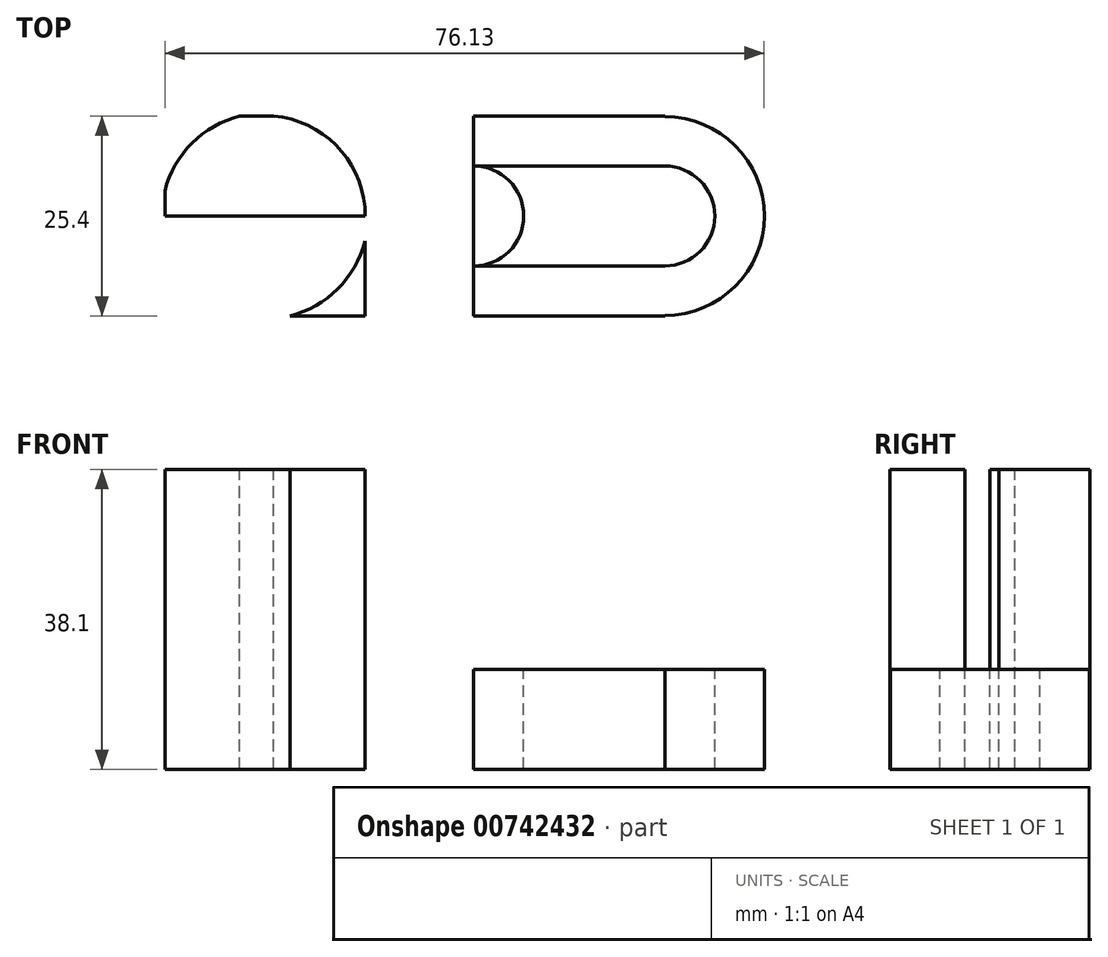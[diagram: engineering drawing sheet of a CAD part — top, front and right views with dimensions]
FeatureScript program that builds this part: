
annotation { "Feature Type Name" : "Feature", "Feature Type Description" : "" }
export const myFeature = defineFeature(function(context is Context, id is Id, definition is map)
    precondition{}
    {
        {
            var Q0;
            Q0=qCreatedBy(makeId("Front.planeOp"),FACE);
            var sketch = newSketch(context, id + "F0", { "sketchPlane" : qUnion([Q0])});
            skLineSegment(sketch, "E0", {"start": v(0, 38.1) * mm, "end": v(0, 0) * mm});
            skLineSegment(sketch, "E1", {"start": v(0, 0) * mm, "end": v(76.2, 0) * mm});
            skLineSegment(sketch, "E2", {"start": v(76.2, 0) * mm, "end": v(76.2, 12.7) * mm});
            skLineSegment(sketch, "E3", {"start": v(76.2, 12.7) * mm, "end": v(25.4, 12.7) * mm});
            skLineSegment(sketch, "E4", {"start": v(25.4, 12.7) * mm, "end": v(25.4, 38.1) * mm});
            skLineSegment(sketch, "E5", {"start": v(25.4, 38.1) * mm, "end": v(0, 38.1) * mm});
            skSolve(sketch);
        }
        {
            var Q0;
            Q0 = qSketchRegion(id + "F0", true);
            extrude(context, id + "F1", {"entities" : qUnion([Q0]), "depth" : 25.4 * mm, "offsetDistance" : 25.4 * mm});
        }
        {
            var Q0;
            Q0=makeQuery(id+"F1.opExtrude","SWEPT_FACE",FACE,{"disambiguationData":[OSD([sQuery(id+"F0.wireOp",EDGE,"E5")])]});
            var sketch = newSketch(context, id + "F2", { "sketchPlane" : qUnion([Q0])});
            skLineSegment(sketch, "E6", {"start": v(12.7, 0) * mm, "end": v(12.7, -25.4) * mm});
            skLineSegment(sketch, "E7", {"start": v(0, -12.7) * mm, "end": v(25.4, -12.7) * mm});
            skCircle(sketch, "E8", {"center": v(12.7, -12.7) * mm, "radius": 13.1 * mm});
            skCircle(sketch, "E9", {"center": v(12.7, -12.7) * mm, "radius": 6.35 * mm});
            skSolve(sketch);
        }
        {
            var Q0;
            {var subQ0=sQuery(id+"F2.wireOp",EDGE,"E9");var subQ1=sQuery(id+"F2.wireOp",EDGE,"E6");var subQ2=makeQuery(id+"F2.imprint","INTERSECT",VERTEX,{"disambiguationData":[OD(0.0)],"derivedFrom":[subQ1,subQ0]});Q0=makeQuery(id+"F2.imprint","IMPRINT",FACE,{"disambiguationData":[TD([[makeQuery(id+"F2.imprint","IMPRINT",EDGE,{"disambiguationData":[TD([[subQ2,-1.0]])],"derivedFrom":subQ1}),-1.0]])]});}
            var Q1;
            {var subQ0=sQuery(id+"F2.wireOp",EDGE,"E9");var subQ1=sQuery(id+"F2.wireOp",EDGE,"E6");var subQ2=makeQuery(id+"F2.imprint","INTERSECT",VERTEX,{"disambiguationData":[OD(0.0)],"derivedFrom":[subQ1,subQ0]});Q1=makeQuery(id+"F2.imprint","IMPRINT",FACE,{"disambiguationData":[TD([[makeQuery(id+"F2.imprint","IMPRINT",EDGE,{"disambiguationData":[TD([[subQ2,-1.0]])],"derivedFrom":subQ1}),1.0]])]});}
            var Q2;
            {var subQ0=sQuery(id+"F2.wireOp",EDGE,"E7");var subQ1=sQuery(id+"F2.wireOp",EDGE,"E6");var subQ2=makeQuery(id+"F2.imprint","INTERSECT",VERTEX,{"derivedFrom":[subQ1,subQ0]});Q2=makeQuery(id+"F2.imprint","IMPRINT",FACE,{"disambiguationData":[TD([[makeQuery(id+"F2.imprint","IMPRINT",EDGE,{"disambiguationData":[TD([[subQ2,-1.0]])],"derivedFrom":subQ1}),1.0]])]});}
            var Q3;
            {var subQ0=sQuery(id+"F2.wireOp",EDGE,"E7");var subQ1=sQuery(id+"F2.wireOp",EDGE,"E6");var subQ2=makeQuery(id+"F2.imprint","INTERSECT",VERTEX,{"derivedFrom":[subQ1,subQ0]});Q3=makeQuery(id+"F2.imprint","IMPRINT",FACE,{"disambiguationData":[TD([[makeQuery(id+"F2.imprint","IMPRINT",EDGE,{"disambiguationData":[TD([[subQ2,-1.0]])],"derivedFrom":subQ1}),-1.0]])]});}
            var Q4;
            {var subQ0=sQuery(id+"F2.wireOp",EDGE,"E8");var subQ1=sQuery(id+"F0.wireOp",EDGE,"E5");var subQ2=makeQuery(id+"F1.opExtrude","CAP_EDGE",EDGE,{"disambiguationData":[OSD([subQ1])],"isStart":true});var subQ3=makeQuery(id+"F2.imprint","INTERSECT",VERTEX,{"disambiguationData":[OD(1.0)],"derivedFrom":[subQ2,subQ0]});Q4=makeQuery(id+"F2.imprint","IMPRINT",FACE,{"disambiguationData":[TD([[makeQuery(id+"F2.imprint","IMPRINT",EDGE,{"disambiguationData":[TD([[subQ3,-1.0]])],"derivedFrom":subQ0}),-1.0]])]});}
            var Q5;
            {var subQ0=sQuery(id+"F2.wireOp",EDGE,"E8");var subQ1=sQuery(id+"F0.wireOp",EDGE,"E5");var subQ4=makeQuery(id+"F1.opExtrude","CAP_EDGE",EDGE,{"disambiguationData":[OSD([subQ1])],"isStart":false});var subQ5=makeQuery(id+"F2.imprint","INTERSECT",VERTEX,{"disambiguationData":[OD(0.0)],"derivedFrom":[subQ4,subQ0]});Q5=makeQuery(id+"F2.imprint","IMPRINT",FACE,{"disambiguationData":[TD([[makeQuery(id+"F2.imprint","IMPRINT",EDGE,{"disambiguationData":[TD([[subQ5,1.0]])],"derivedFrom":subQ0}),-1.0]])]});}
            extrude(context, id + "F3", {"entities" : qUnion([Q0, Q1, Q2, Q3, Q4, Q5]), "operationType" : NewBodyOperationType.REMOVE, "endBound" : BoundingType.THROUGH_ALL, "oppositeDirection" : true, "depth" : 25.4 * mm, "offsetDistance" : 25.4 * mm});
        }
        {
            var Q0;
            Q0=makeQuery(id+"F1.opExtrude","SWEPT_FACE",FACE,{"disambiguationData":[OSD([sQuery(id+"F0.wireOp",EDGE,"E5")])]});
            var sketch = newSketch(context, id + "F4", { "sketchPlane" : qUnion([Q0])});
            skLineSegment(sketch, "E10", {"start": v(0, 0) * mm, "end": v(12.7, 0) * mm});
            skLineSegment(sketch, "E11", {"start": v(12.7, 0) * mm, "end": v(12.7, -25.4) * mm});
            skLineSegment(sketch, "E12", {"start": v(0, -12.7) * mm, "end": v(25.4, -12.7) * mm});
            skCircle(sketch, "E13", {"center": v(12.7, -12.7) * mm, "radius": 12.75 * mm});
            skSolve(sketch);
        }
        {
            var Q0;
            {var subQ0=sQuery(id+"F4.wireOp",EDGE,"E13");var subQ1=sQuery(id+"F0.wireOp",EDGE,"E5");var subQ2=makeQuery(id+"F1.opExtrude","CAP_EDGE",EDGE,{"disambiguationData":[OSD([subQ1])],"isStart":false});var subQ3=makeQuery(id+"F4.imprint","INTERSECT",VERTEX,{"disambiguationData":[OD(1.0)],"derivedFrom":[subQ2,subQ0]});Q0=makeQuery(id+"F4.imprint","IMPRINT",FACE,{"disambiguationData":[TD([[makeQuery(id+"F4.imprint","IMPRINT",EDGE,{"disambiguationData":[TD([[subQ3,-1.0]])],"derivedFrom":subQ0}),-1.0]])]});}
            var Q1;
            {var subQ0=sQuery(id+"F4.wireOp",EDGE,"E13");var subQ1=sQuery(id+"F0.wireOp",EDGE,"E5");var subQ2=makeQuery(id+"F1.opExtrude","CAP_EDGE",EDGE,{"disambiguationData":[OSD([subQ1])],"isStart":true});var subQ3=makeQuery(id+"F4.imprint","INTERSECT",VERTEX,{"derivedFrom":[subQ2,subQ0]});Q1=makeQuery(id+"F4.imprint","IMPRINT",FACE,{"disambiguationData":[TD([[makeQuery(id+"F4.imprint","IMPRINT",EDGE,{"disambiguationData":[TD([[subQ3,1.0]])],"derivedFrom":subQ0}),-1.0]])]});}
            extrude(context, id + "F5", {"entities" : qUnion([Q0, Q1]), "operationType" : NewBodyOperationType.REMOVE, "oppositeDirection" : true, "depth" : 25.4 * mm, "offsetDistance" : 25.4 * mm});
        }
        {
            var Q0;
            {var subQ0=sQuery(id+"F0.wireOp",EDGE,"E5");var subQ1=makeQuery(id+"F1.opExtrude","CAP_EDGE",EDGE,{"disambiguationData":[OSD([subQ0])],"isStart":false});var subQ2=sQuery(id+"F0.wireOp",EDGE,"E4");var subQ3=makeQuery(id+"F1.opExtrude","SWEPT_EDGE",EDGE,{"disambiguationData":[OSD([subQ2,subQ0])]});var subQ4=makeQuery(id+"F4.imprint","INTERSECT",VERTEX,{"derivedFrom":[subQ3,subQ1]});var subQ5=sQuery(id+"F4.wireOp",EDGE,"E13");var subQ6=makeQuery(id+"F4.imprint","INTERSECT",VERTEX,{"disambiguationData":[OD(1.0)],"derivedFrom":[subQ1,subQ5]});var subQ8=makeQuery(id+"F1.opExtrude","CAP_EDGE",EDGE,{"disambiguationData":[OSD([subQ0])],"isStart":true});var subQ9=makeQuery(id+"F4.imprint","INTERSECT",VERTEX,{"derivedFrom":[subQ3,subQ8]});var subQ10=makeQuery(id+"F4.imprint","INTERSECT",VERTEX,{"derivedFrom":[subQ8,subQ5]});Q0=makeQuery(id+"F5.boolean.opBoolean","MERGE",FACE,{"derivedFrom":[makeQuery(id+"F1.opExtrude","SWEPT_FACE",FACE,{"disambiguationData":[OSD([sQuery(id+"F0.wireOp",EDGE,"E3")])]}),makeQuery(id+"F5.opExtrude","CAP_FACE",FACE,{"disambiguationData":[OSD([subQ2,subQ0,subQ5]),TDD([makeQuery(id+"F4.imprint","IMPRINT",EDGE,{"disambiguationData":[TD([[subQ10,1.0]])],"derivedFrom":subQ5}),makeQuery(id+"F4.imprint","IMPRINT",EDGE,{"disambiguationData":[TD([[subQ9,1.0]])],"derivedFrom":subQ3}),makeQuery(id+"F4.imprint","IMPRINT",EDGE,{"disambiguationData":[TD([[subQ10,1.0]])],"derivedFrom":subQ8})])],"isStart":false}),makeQuery(id+"F5.opExtrude","CAP_FACE",FACE,{"disambiguationData":[OSD([subQ2,subQ0,subQ5]),TDD([makeQuery(id+"F4.imprint","IMPRINT",EDGE,{"disambiguationData":[TD([[subQ6,-1.0]])],"derivedFrom":subQ5}),makeQuery(id+"F4.imprint","IMPRINT",EDGE,{"disambiguationData":[TD([[subQ4,-1.0]])],"derivedFrom":subQ3}),makeQuery(id+"F4.imprint","IMPRINT",EDGE,{"disambiguationData":[TD([[subQ6,1.0]])],"derivedFrom":subQ1})])],"isStart":false})]});}
            var sketch = newSketch(context, id + "F6", { "sketchPlane" : qUnion([Q0])});
            skLineSegment(sketch, "E14", {"start": v(76.2, -12.7) * mm, "end": v(25.4, -12.7) * mm});
            skLineSegment(sketch, "E15", {"start": v(39.23, 0) * mm, "end": v(39.23, -25.4) * mm});
            skLineSegment(sketch, "E16", {"start": v(63.5, 0) * mm, "end": v(63.5, -25.4) * mm});
            skCircle(sketch, "E17", {"center": v(39.23, -12.7) * mm, "radius": 6.35 * mm});
            skCircle(sketch, "E18", {"center": v(63.5, -12.7) * mm, "radius": 6.35 * mm});
            skCircle(sketch, "E19", {"center": v(63.5, -12.7) * mm, "radius": 12.63 * mm});
            skLineSegment(sketch, "E20", {"start": v(39.23, -6.35) * mm, "end": v(63.5, -6.35) * mm});
            skLineSegment(sketch, "E21", {"start": v(39.23, -19.05) * mm, "end": v(63.5, -19.05) * mm});
            skSolve(sketch);
        }
        {
            var Q0;
            {var subQ0=sQuery(id+"F6.wireOp",EDGE,"E15");var subQ1=sQuery(id+"F6.wireOp",EDGE,"E14");var subQ2=makeQuery(id+"F6.imprint","INTERSECT",VERTEX,{"derivedFrom":[subQ1,subQ0]});Q0=makeQuery(id+"F6.imprint","IMPRINT",FACE,{"disambiguationData":[TD([[makeQuery(id+"F6.imprint","IMPRINT",EDGE,{"disambiguationData":[TD([[subQ2,-1.0]])],"derivedFrom":subQ1}),-1.0]])]});}
            var Q1;
            {var subQ0=sQuery(id+"F6.wireOp",EDGE,"E17");var subQ1=sQuery(id+"F6.wireOp",EDGE,"E14");var subQ2=makeQuery(id+"F6.imprint","INTERSECT",VERTEX,{"disambiguationData":[OD(0.0)],"derivedFrom":[subQ1,subQ0]});Q1=makeQuery(id+"F6.imprint","IMPRINT",FACE,{"disambiguationData":[TD([[makeQuery(id+"F6.imprint","IMPRINT",EDGE,{"disambiguationData":[TD([[subQ2,-1.0]])],"derivedFrom":subQ1}),-1.0]])]});}
            var Q2;
            {var subQ0=sQuery(id+"F6.wireOp",EDGE,"E17");var subQ1=sQuery(id+"F6.wireOp",EDGE,"E14");var subQ2=makeQuery(id+"F6.imprint","INTERSECT",VERTEX,{"disambiguationData":[OD(0.0)],"derivedFrom":[subQ1,subQ0]});Q2=makeQuery(id+"F6.imprint","IMPRINT",FACE,{"disambiguationData":[TD([[makeQuery(id+"F6.imprint","IMPRINT",EDGE,{"disambiguationData":[TD([[subQ2,-1.0]])],"derivedFrom":subQ1}),1.0]])]});}
            var Q3;
            {var subQ0=sQuery(id+"F6.wireOp",EDGE,"E15");var subQ1=sQuery(id+"F6.wireOp",EDGE,"E14");var subQ2=makeQuery(id+"F6.imprint","INTERSECT",VERTEX,{"derivedFrom":[subQ1,subQ0]});Q3=makeQuery(id+"F6.imprint","IMPRINT",FACE,{"disambiguationData":[TD([[makeQuery(id+"F6.imprint","IMPRINT",EDGE,{"disambiguationData":[TD([[subQ2,-1.0]])],"derivedFrom":subQ1}),1.0]])]});}
            var Q4;
            {var subQ0=sQuery(id+"F6.wireOp",EDGE,"E19");var subQ1=sQuery(id+"F6.wireOp",EDGE,"E14");var subQ2=makeQuery(id+"F6.imprint","INTERSECT",VERTEX,{"disambiguationData":[OD(1.0)],"derivedFrom":[subQ1,subQ0]});Q4=makeQuery(id+"F6.imprint","IMPRINT",FACE,{"disambiguationData":[TD([[makeQuery(id+"F6.imprint","IMPRINT",EDGE,{"disambiguationData":[TD([[subQ2,-1.0]])],"derivedFrom":subQ1}),-1.0]])]});}
            var Q5;
            {var subQ0=sQuery(id+"F6.wireOp",EDGE,"E18");var subQ1=sQuery(id+"F6.wireOp",EDGE,"E14");var subQ2=makeQuery(id+"F6.imprint","INTERSECT",VERTEX,{"disambiguationData":[OD(1.0)],"derivedFrom":[subQ1,subQ0]});Q5=makeQuery(id+"F6.imprint","IMPRINT",FACE,{"disambiguationData":[TD([[makeQuery(id+"F6.imprint","IMPRINT",EDGE,{"disambiguationData":[TD([[subQ2,-1.0]])],"derivedFrom":subQ1}),-1.0]])]});}
            var Q6;
            {var subQ0=sQuery(id+"F6.wireOp",EDGE,"E18");var subQ1=sQuery(id+"F6.wireOp",EDGE,"E14");var subQ2=makeQuery(id+"F6.imprint","INTERSECT",VERTEX,{"disambiguationData":[OD(1.0)],"derivedFrom":[subQ1,subQ0]});Q6=makeQuery(id+"F6.imprint","IMPRINT",FACE,{"disambiguationData":[TD([[makeQuery(id+"F6.imprint","IMPRINT",EDGE,{"disambiguationData":[TD([[subQ2,-1.0]])],"derivedFrom":subQ1}),1.0]])]});}
            var Q7;
            {var subQ0=sQuery(id+"F6.wireOp",EDGE,"E16");var subQ1=sQuery(id+"F6.wireOp",EDGE,"E14");var subQ2=makeQuery(id+"F6.imprint","INTERSECT",VERTEX,{"derivedFrom":[subQ1,subQ0]});Q7=makeQuery(id+"F6.imprint","IMPRINT",FACE,{"disambiguationData":[TD([[makeQuery(id+"F6.imprint","IMPRINT",EDGE,{"disambiguationData":[TD([[subQ2,-1.0]])],"derivedFrom":subQ1}),1.0]])]});}
            var Q8;
            {var subQ0=sQuery(id+"F6.wireOp",EDGE,"E18");var subQ1=sQuery(id+"F6.wireOp",EDGE,"E14");var subQ2=makeQuery(id+"F6.imprint","INTERSECT",VERTEX,{"disambiguationData":[OD(0.0)],"derivedFrom":[subQ1,subQ0]});Q8=makeQuery(id+"F6.imprint","IMPRINT",FACE,{"disambiguationData":[TD([[makeQuery(id+"F6.imprint","IMPRINT",EDGE,{"disambiguationData":[TD([[subQ2,-1.0]])],"derivedFrom":subQ1}),1.0]])]});}
            var Q9;
            {var subQ0=sQuery(id+"F6.wireOp",EDGE,"E16");var subQ1=sQuery(id+"F6.wireOp",EDGE,"E14");var subQ2=makeQuery(id+"F6.imprint","INTERSECT",VERTEX,{"derivedFrom":[subQ1,subQ0]});Q9=makeQuery(id+"F6.imprint","IMPRINT",FACE,{"disambiguationData":[TD([[makeQuery(id+"F6.imprint","IMPRINT",EDGE,{"disambiguationData":[TD([[subQ2,-1.0]])],"derivedFrom":subQ1}),-1.0]])]});}
            var Q10;
            {var subQ0=sQuery(id+"F6.wireOp",EDGE,"E18");var subQ1=sQuery(id+"F6.wireOp",EDGE,"E14");var subQ2=makeQuery(id+"F6.imprint","INTERSECT",VERTEX,{"disambiguationData":[OD(0.0)],"derivedFrom":[subQ1,subQ0]});Q10=makeQuery(id+"F6.imprint","IMPRINT",FACE,{"disambiguationData":[TD([[makeQuery(id+"F6.imprint","IMPRINT",EDGE,{"disambiguationData":[TD([[subQ2,-1.0]])],"derivedFrom":subQ1}),-1.0]])]});}
            var Q11;
            {var subQ6=sQuery(id+"F6.wireOp",EDGE,"E14");var subQ8=sQuery(id+"F6.wireOp",EDGE,"E19");var subQ9=makeQuery(id+"F6.imprint","INTERSECT",VERTEX,{"disambiguationData":[OD(0.0)],"derivedFrom":[subQ6,subQ8]});Q11=makeQuery(id+"F6.imprint","IMPRINT",FACE,{"disambiguationData":[TD([[makeQuery(id+"F6.imprint","IMPRINT",EDGE,{"disambiguationData":[TD([[subQ9,-1.0]])],"derivedFrom":subQ8}),-1.0]])]});}
            var Q12;
            {var subQ0=sQuery(id+"F6.wireOp",EDGE,"E19");var subQ1=sQuery(id+"F6.wireOp",EDGE,"E14");var subQ2=makeQuery(id+"F6.imprint","INTERSECT",VERTEX,{"disambiguationData":[OD(0.0)],"derivedFrom":[subQ1,subQ0]});Q12=makeQuery(id+"F6.imprint","IMPRINT",FACE,{"disambiguationData":[TD([[makeQuery(id+"F6.imprint","IMPRINT",EDGE,{"disambiguationData":[TD([[subQ2,1.0]])],"derivedFrom":subQ0}),-1.0]])]});}
            var Q13;
            {var subQ0=sQuery(id+"F6.wireOp",EDGE,"E19");var subQ1=sQuery(id+"F6.wireOp",EDGE,"E14");var subQ2=makeQuery(id+"F6.imprint","INTERSECT",VERTEX,{"disambiguationData":[OD(1.0)],"derivedFrom":[subQ1,subQ0]});Q13=makeQuery(id+"F6.imprint","IMPRINT",FACE,{"disambiguationData":[TD([[makeQuery(id+"F6.imprint","IMPRINT",EDGE,{"disambiguationData":[TD([[subQ2,-1.0]])],"derivedFrom":subQ1}),1.0]])]});}
            extrude(context, id + "F7", {"entities" : qUnion([Q0, Q1, Q2, Q3, Q4, Q5, Q6, Q7, Q8, Q9, Q10, Q11, Q12, Q13]), "operationType" : NewBodyOperationType.REMOVE, "oppositeDirection" : true, "depth" : 25.4 * mm, "offsetDistance" : 25.4 * mm});
        }
    });
